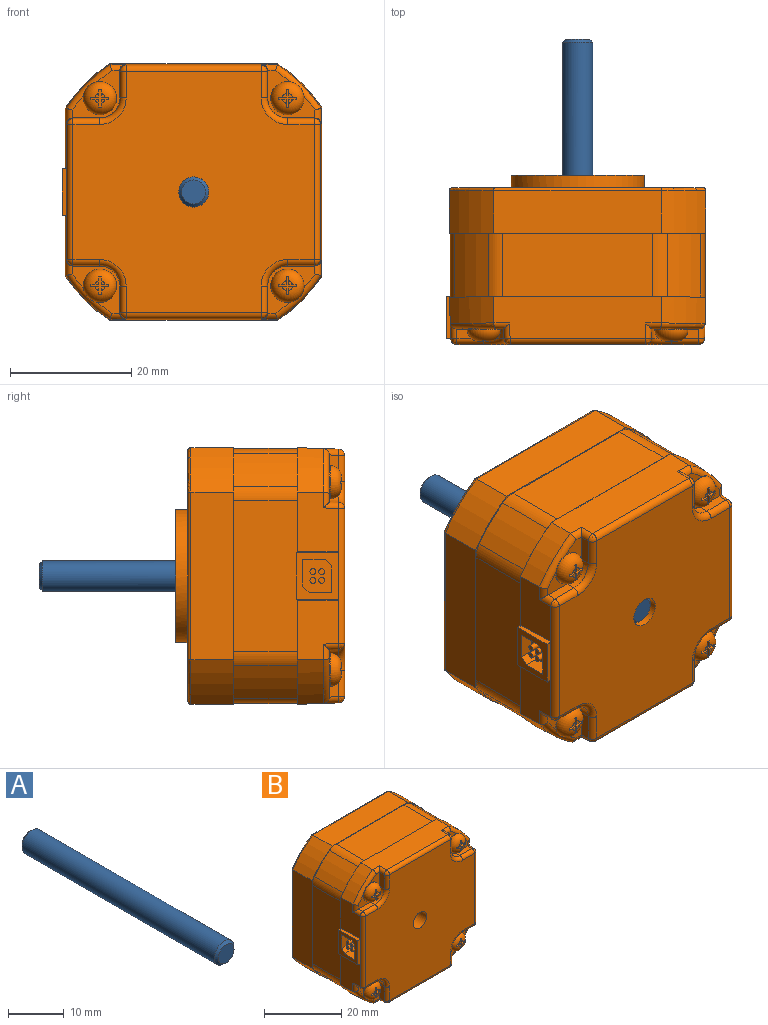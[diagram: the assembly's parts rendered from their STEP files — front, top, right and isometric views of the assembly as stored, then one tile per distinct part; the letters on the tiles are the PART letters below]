
ASSEMBLY  parts=2 mates=1
PART A: 5 faces, bbox 5x49.8x5 mm
  f0: cone r=1mm half-angle=45deg, axis (0,-1,0), area 10.1mm2, adj f2,f3
  f1: cone r=1mm half-angle=45deg, axis (0,1,0), area 10.1mm2, adj f2,f4
  f2: cylinder r=2.5mm len=48.77mm, axis (0,1,0), area 764.7mm2, adj f0,f1
  f3: plane 3.98x3.98mm, normal (0,1,0), area 12.4mm2, adj f0
  f4: plane 3.98x3.98mm, normal (0,-1,0), area 12.4mm2, adj f1
PART B: 249 faces, bbox 46x28.1x46 mm
  f0: cylinder r=0.48mm len=1.93mm, axis (1,0,0), area 5.9mm2, adj f1,f2
  f1: plane 0.97x0.97mm, normal (-1,0,0), area 0.7mm2, adj f0
  f2: plane 5.49x4.85mm, normal (-1,0,0), area 22.5mm2, adj f0,f3,f5,f7,f9,f244,f245,f246
  f3: cylinder r=0.48mm len=1.93mm, axis (1,0,0), area 5.9mm2, adj f2,f4
  f4: plane 0.97x0.97mm, normal (-1,0,0), area 0.7mm2, adj f3
  f5: cylinder r=0.48mm len=1.93mm, axis (1,0,0), area 5.9mm2, adj f2,f6
  f6: plane 0.97x0.97mm, normal (-1,0,0), area 0.7mm2, adj f5
  f7: cylinder r=0.48mm len=1.93mm, axis (1,0,0), area 5.9mm2, adj f2,f8
  f8: plane 0.97x0.97mm, normal (-1,0,0), area 0.7mm2, adj f7
  f9: plane 3.77x2.36mm, normal (0,0,-1), area 8.9mm2, adj f2,f10,f244,f248
  f10: plane 7.62x6.99mm, normal (-1,0,0), area 27.8mm2, adj f9,f11,f241,f242,f243,f244,f245,f246
  f11: plane 7.62x0.79mm, normal (0,-1,0), area 6mm2, adj f10,f12,f241,f243
  f12: plane 27.77x6.84mm, normal (-1,-0.03,0), area 121.2mm2, adj f11,f13,f230,f231,f232,f233,f234,f235
  f13: plane 6.61x1.82mm, normal (0,0,-1), area 11.2mm2, adj f12,f14,f15,f237,f240
  f14: plane 6.61x0.25mm, normal (-1,0,0), area 1.7mm2, adj f13,f15,f240,f243
  f15: plane 1.69x0.25mm, normal (0,-1,0), area 0.4mm2, adj f13,f14,f16,f243
  f16: plane 24.85x10.52mm, normal (-1,0,0), area 261.3mm2, adj f15,f17,f224,f225,f227,f229,f237
  f17: plane 42.42x42.42mm, normal (0,-1,0), area 24.6mm2, adj f16,f18,f19,f20,f21,f22,f23,f24
  f18: cylinder r=25.13mm len=10.52mm, axis (0,1,0), area 82.5mm2, adj f17,f19,f229,f237
  f19: cylinder r=4.01mm len=10.52mm, axis (0,1,0), area 26.6mm2, adj f17,f18,f20,f237
  f20: plane 24.85x10.52mm, normal (0,0,-1), area 261.3mm2, adj f17,f19,f21,f237
  f21: cylinder r=4.01mm len=10.52mm, axis (0,1,0), area 26.6mm2, adj f17,f20,f22,f237
  f22: cylinder r=25.13mm len=10.52mm, axis (0,1,0), area 82.5mm2, adj f17,f21,f23,f237
  f23: cylinder r=4.01mm len=10.52mm, axis (0,1,0), area 26.6mm2, adj f17,f22,f24,f237
  f24: plane 24.85x10.52mm, normal (1,0,0), area 261.3mm2, adj f17,f23,f25,f237
  f25: cylinder r=4.01mm len=10.52mm, axis (0,1,0), area 26.6mm2, adj f17,f24,f26,f237
  f26: cylinder r=25.13mm len=10.52mm, axis (0,1,0), area 82.5mm2, adj f17,f25,f27,f237
  f27: cylinder r=4.01mm len=10.52mm, axis (0,1,0), area 26.6mm2, adj f17,f26,f28,f237
  f28: plane 24.85x10.52mm, normal (0,0,1), area 261.3mm2, adj f17,f27,f29,f237
  f29: cylinder r=4.01mm len=10.52mm, axis (0,1,0), area 26.6mm2, adj f17,f28,f30,f237
  f30: cylinder r=25.13mm len=10.52mm, axis (0,1,0), area 82.5mm2, adj f17,f29,f224,f237
  f31: plane 27.77x7.06mm, normal (0,0,1), area 196.1mm2, adj f17,f32,f217,f223
  f32: cylinder r=0.51mm len=27.77mm, axis (1,0,0), area 22mm2, adj f31,f33,f39,f216
  f33: torus R=24.84mm, axis (0,1,0), area 8.1mm2, adj f32,f34,f39,f223
  f34: cylinder r=0.51mm len=27.77mm, axis (0,0,1), area 22mm2, adj f33,f35,f39,f222
  f35: torus R=24.84mm, axis (0,1,0), area 8.1mm2, adj f34,f36,f39,f221
  f36: cylinder r=0.51mm len=27.77mm, axis (-1,0,0), area 22mm2, adj f35,f37,f39,f220
  f37: torus R=24.84mm, axis (0,1,0), area 8.1mm2, adj f36,f38,f39,f219
  f38: cylinder r=0.51mm len=27.77mm, axis (0,0,-1), area 22mm2, adj f37,f39,f216,f218
  f39: plane 41.4x41.4mm, normal (0,1,0), area 1030.3mm2, adj f32,f33,f34,f35,f36,f37,f38,f40
  f40: cone r=1mm half-angle=45deg, axis (0,1,0), area 2.6mm2, adj f39,f41,f44,f45,f46
  f41: cylinder r=1.23mm len=3.49mm, axis (0,1,0), area -38.1mm2, adj f40,f42,f43,f44,f46
  f42: bspline ~3.05x3.05mm, area 6.4mm2, adj f41,f43,f45
  f43: plane 2.86x2.83mm, normal (0,1,0), area 5.7mm2, adj f41,f42,f45,f46
  f44: bspline ~3.04x3.03mm, area 5.1mm2, adj f40,f41,f45
  f45: cylinder r=1.5mm len=3.76mm, axis (0,1,0), area 3.8mm2, adj f40,f42,f43,f44,f46
  f46: bspline ~4.17x3.53mm, area 17.6mm2, adj f40,f41,f43,f45
  f47: cone r=1mm half-angle=45deg, axis (0,1,0), area 2.6mm2, adj f39,f48,f51,f52,f53
  f48: cylinder r=1.23mm len=3.49mm, axis (0,1,0), area -38.1mm2, adj f47,f49,f50,f51,f53
  f49: bspline ~3.05x3.05mm, area 6.4mm2, adj f48,f50,f52
  f50: plane 2.86x2.83mm, normal (0,1,0), area 5.7mm2, adj f48,f49,f52,f53
  f51: bspline ~3.04x3.03mm, area 5.1mm2, adj f47,f48,f52
  f52: cylinder r=1.5mm len=3.76mm, axis (0,1,0), area 3.8mm2, adj f47,f49,f50,f51,f53
  f53: bspline ~4.17x3.53mm, area 17.6mm2, adj f47,f48,f50,f52
  f54: cone r=1mm half-angle=45deg, axis (0,1,0), area 2.6mm2, adj f39,f55,f58,f59,f60
  f55: cylinder r=1.23mm len=3.49mm, axis (0,1,0), area -38.1mm2, adj f54,f56,f57,f58,f60
  f56: bspline ~3.05x3.05mm, area 6.4mm2, adj f55,f57,f59
  f57: plane 2.86x2.83mm, normal (0,1,0), area 5.7mm2, adj f55,f56,f59,f60
  f58: bspline ~3.04x3.03mm, area 5.1mm2, adj f54,f55,f59
  f59: cylinder r=1.5mm len=3.76mm, axis (0,1,0), area 3.8mm2, adj f54,f56,f57,f58,f60
  f60: bspline ~4.17x3.53mm, area 17.6mm2, adj f54,f55,f57,f59
  f61: cylinder r=13.46mm len=26.92mm, axis (0,1,0), area 43mm2, adj f39,f62
  f62: plane 26.92x26.92mm, normal (0,1,0), area 189.3mm2, adj f61,f63
  f63: cylinder r=11mm len=22mm, axis (0,-1,0), area 175.5mm2, adj f62,f64
  f64: plane 22x22mm, normal (0,1,0), area 314.3mm2, adj f63,f65
  f65: cylinder r=4.57mm len=9.14mm, axis (0,1,0), area 58.4mm2, adj f64,f66
  f66: plane 9.14x9.14mm, normal (0,1,0), area 46.1mm2, adj f65,f67
  f67: cylinder r=2.5mm len=25.91mm, axis (0,1,0), area 406.2mm2, adj f66,f68
  f68: plane 39.91x39.91mm, normal (0,-1,0), area 1280.7mm2, adj f67,f69,f193,f194,f195,f196,f198,f200
  f69: cylinder r=1.02mm len=4.42mm, axis (0,0,1), area 6.9mm2, adj f68,f70,f192,f208
  f70: plane 4.47x1.56mm, normal (1,-0.03,0), area 6.9mm2, adj f69,f71,f190,f191
  f71: plane 7.81x7.81mm, normal (0,-1,0), area 17.4mm2, adj f70,f72,f165,f166,f168,f169,f189,f190
  f72: cylinder r=1.02mm len=2.58mm, axis (-1,0,0), area 3mm2, adj f71,f73,f189,f190
  f73: plane 27.77x6.84mm, normal (0,-0.03,-1), area 176.3mm2, adj f72,f74,f100,f102,f190,f193,f236,f237
  f74: cylinder r=1.02mm len=2.58mm, axis (-1,0,0), area 3mm2, adj f73,f75,f99,f100
  f75: plane 7.81x7.81mm, normal (0,-1,0), area 17.4mm2, adj f74,f76,f77,f78,f79,f99,f100,f234
  f76: plane 4.47x1.56mm, normal (0,-0.03,-1), area 6.9mm2, adj f75,f77,f196,f234
  f77: cone r=0.03mm half-angle=2deg, axis (0,-1,0), area 8.2mm2, adj f75,f76,f78,f195
  f78: plane 4.47x1.56mm, normal (-1,-0.03,0), area 6.9mm2, adj f75,f77,f100,f194
  f79: cylinder r=2.75mm len=5.5mm, axis (0,1,0), area 2.2mm2, adj f75,f80,f98
  f80: torus R=0.84mm, axis (0,1,0), area 37.5mm2, adj f79,f81,f83,f84,f85,f86,f87,f88
  f81: plane 1.56x1.33mm, normal (-1,0,0), area 1.9mm2, adj f80,f82,f83,f84,f97
  f82: plane 3x3mm, normal (0,-1,0), area 2.3mm2, adj f81,f84,f85,f86,f88,f89,f90,f92
  f83: plane 0.62x0.62mm, normal (0,-1,0), area 0.3mm2, adj f80,f81,f84
  f84: plane 1.56x1.33mm, normal (0,0,1), area 1.9mm2, adj f80,f81,f82,f83,f85
  f85: plane 1.44x0.44mm, normal (-1,0,0), area 0.6mm2, adj f80,f82,f84,f86
  f86: plane 1.56x1.33mm, normal (0,0,-1), area 1.9mm2, adj f80,f82,f85,f87,f88
  f87: plane 0.62x0.62mm, normal (0,-1,0), area 0.3mm2, adj f80,f86,f88
  f88: plane 1.56x1.33mm, normal (-1,0,0), area 1.9mm2, adj f80,f82,f86,f87,f89
  f89: plane 1.42x0.41mm, normal (0,0,-1), area 0.6mm2, adj f80,f82,f88,f90
  f90: plane 1.56x1.33mm, normal (1,0,0), area 1.9mm2, adj f80,f82,f89,f91,f92
  f91: plane 0.62x0.62mm, normal (0,-1,0), area 0.3mm2, adj f80,f90,f92
  f92: plane 1.56x1.33mm, normal (0,0,-1), area 1.9mm2, adj f80,f82,f90,f91,f93
  f93: plane 1.44x0.44mm, normal (1,0,0), area 0.6mm2, adj f80,f82,f92,f94
  f94: plane 1.56x1.33mm, normal (0,0,1), area 1.9mm2, adj f80,f82,f93,f95,f96
  f95: plane 0.62x0.62mm, normal (0,-1,0), area 0.3mm2, adj f80,f94,f96
  f96: plane 1.56x1.33mm, normal (1,0,0), area 1.9mm2, adj f80,f82,f94,f95,f97
  f97: plane 1.42x0.41mm, normal (0,0,1), area 0.6mm2, adj f80,f81,f82,f96
  f98: plane 2.3x2.3mm, normal (0,1,0), area 1.1mm2, adj f79,f99
  f99: torus R=24.18mm, axis (0,1,0), area 15.3mm2, adj f74,f75,f98,f235,f236
  f100: cylinder r=1.02mm len=2.55mm, axis (-0.03,1,-0.03), area 3.1mm2, adj f73,f74,f75,f78,f101
  f101: sphere r=1.02mm, area 1mm2, adj f100,f193,f194
  f102: cone r=0.03mm half-angle=2deg, axis (0,1,0), area 44.6mm2, adj f73,f103,f189,f237
  f103: plane 27.77x6.84mm, normal (1,-0.03,0), area 176.3mm2, adj f102,f104,f163,f164,f166,f168,f206,f237
  f104: cylinder r=1.02mm len=2.55mm, axis (-0.03,-1,-0.03), area 3.1mm2, adj f103,f105,f106,f162,f163
  f105: sphere r=1.02mm, area 1mm2, adj f104,f205,f206
  f106: plane 4.47x1.56mm, normal (0,-0.03,1), area 6.9mm2, adj f104,f107,f162,f205
  f107: cone r=0.03mm half-angle=2deg, axis (0,-1,0), area 8.2mm2, adj f106,f108,f162,f204
  f108: plane 4.47x1.56mm, normal (1,-0.03,0), area 6.9mm2, adj f107,f109,f162,f203
  f109: cylinder r=1.02mm len=2.55mm, axis (0.03,1,0.03), area 3.1mm2, adj f108,f110,f111,f140,f162
  f110: sphere r=1.02mm, area 1mm2, adj f109,f202,f203
  f111: plane 27.77x6.84mm, normal (0,-0.03,1), area 176.3mm2, adj f109,f112,f139,f140,f164,f202,f230,f237
  f112: cylinder r=1.02mm len=2.55mm, axis (0.03,-1,-0.03), area 3.1mm2, adj f111,f113,f114,f117,f139
  f113: sphere r=1.02mm, area 1mm2, adj f112,f201,f202
  f114: plane 4.47x1.56mm, normal (-1,-0.03,0), area 6.9mm2, adj f112,f115,f117,f201
  f115: cone r=0.03mm half-angle=2deg, axis (0,-1,0), area 8.2mm2, adj f114,f116,f117,f200
  f116: plane 4.47x1.56mm, normal (0,-0.03,1), area 6.9mm2, adj f115,f117,f198,f232
  f117: plane 7.81x7.81mm, normal (0,-1,0), area 17.4mm2, adj f112,f114,f115,f116,f118,f138,f139,f231
  f118: cylinder r=2.75mm len=5.5mm, axis (0,1,0), area 2.2mm2, adj f117,f119,f137
  f119: torus R=0.84mm, axis (0,1,0), area 37.5mm2, adj f118,f120,f122,f123,f124,f125,f126,f127
  f120: plane 1.56x1.33mm, normal (-1,0,0), area 1.9mm2, adj f119,f121,f122,f123,f136
  f121: plane 3x3mm, normal (0,-1,0), area 2.3mm2, adj f120,f123,f124,f125,f127,f128,f129,f131
  f122: plane 0.62x0.62mm, normal (0,-1,0), area 0.3mm2, adj f119,f120,f123
  f123: plane 1.56x1.33mm, normal (0,0,1), area 1.9mm2, adj f119,f120,f121,f122,f124
  f124: plane 1.44x0.44mm, normal (-1,0,0), area 0.6mm2, adj f119,f121,f123,f125
  f125: plane 1.56x1.33mm, normal (0,0,-1), area 1.9mm2, adj f119,f121,f124,f126,f127
  f126: plane 0.62x0.62mm, normal (0,-1,0), area 0.3mm2, adj f119,f125,f127
  f127: plane 1.56x1.33mm, normal (-1,0,0), area 1.9mm2, adj f119,f121,f125,f126,f128
  f128: plane 1.42x0.41mm, normal (0,0,-1), area 0.6mm2, adj f119,f121,f127,f129
  f129: plane 1.56x1.33mm, normal (1,0,0), area 1.9mm2, adj f119,f121,f128,f130,f131
  f130: plane 0.62x0.62mm, normal (0,-1,0), area 0.3mm2, adj f119,f129,f131
  f131: plane 1.56x1.33mm, normal (0,0,-1), area 1.9mm2, adj f119,f121,f129,f130,f132
  f132: plane 1.44x0.44mm, normal (1,0,0), area 0.6mm2, adj f119,f121,f131,f133
  f133: plane 1.56x1.33mm, normal (0,0,1), area 1.9mm2, adj f119,f121,f132,f134,f135
  f134: plane 0.62x0.62mm, normal (0,-1,0), area 0.3mm2, adj f119,f133,f135
  f135: plane 1.56x1.33mm, normal (1,0,0), area 1.9mm2, adj f119,f121,f133,f134,f136
  f136: plane 1.42x0.41mm, normal (0,0,1), area 0.6mm2, adj f119,f120,f121,f135
  f137: plane 2.3x2.3mm, normal (0,1,0), area 1.1mm2, adj f118,f138
  f138: torus R=24.18mm, axis (0,-1,0), area 15.3mm2, adj f117,f137,f139,f230,f231
  f139: cylinder r=1.02mm len=2.58mm, axis (1,0,0), area 3mm2, adj f111,f112,f117,f138
  f140: cylinder r=1.02mm len=2.58mm, axis (1,0,0), area 3mm2, adj f109,f111,f141,f162
  f141: torus R=24.18mm, axis (0,-1,0), area 15.3mm2, adj f140,f142,f162,f163,f164
  f142: plane 2.3x2.3mm, normal (0,1,0), area 1.1mm2, adj f141,f143
  f143: cylinder r=2.75mm len=5.5mm, axis (0,1,0), area 2.2mm2, adj f142,f144,f162
  f144: torus R=0.84mm, axis (0,1,0), area 37.5mm2, adj f143,f145,f147,f148,f149,f150,f151,f152
  f145: plane 1.56x1.33mm, normal (-1,0,0), area 1.9mm2, adj f144,f146,f147,f148,f161
  f146: plane 3x3mm, normal (0,-1,0), area 2.3mm2, adj f145,f148,f149,f150,f152,f153,f154,f156
  f147: plane 0.62x0.62mm, normal (0,-1,0), area 0.3mm2, adj f144,f145,f148
  f148: plane 1.56x1.33mm, normal (0,0,1), area 1.9mm2, adj f144,f145,f146,f147,f149
  f149: plane 1.44x0.44mm, normal (-1,0,0), area 0.6mm2, adj f144,f146,f148,f150
  f150: plane 1.56x1.33mm, normal (0,0,-1), area 1.9mm2, adj f144,f146,f149,f151,f152
  f151: plane 0.62x0.62mm, normal (0,-1,0), area 0.3mm2, adj f144,f150,f152
  f152: plane 1.56x1.33mm, normal (-1,0,0), area 1.9mm2, adj f144,f146,f150,f151,f153
  f153: plane 1.42x0.41mm, normal (0,0,-1), area 0.6mm2, adj f144,f146,f152,f154
  f154: plane 1.56x1.33mm, normal (1,0,0), area 1.9mm2, adj f144,f146,f153,f155,f156
  f155: plane 0.62x0.62mm, normal (0,-1,0), area 0.3mm2, adj f144,f154,f156
  f156: plane 1.56x1.33mm, normal (0,0,-1), area 1.9mm2, adj f144,f146,f154,f155,f157
  f157: plane 1.44x0.44mm, normal (1,0,0), area 0.6mm2, adj f144,f146,f156,f158
  f158: plane 1.56x1.33mm, normal (0,0,1), area 1.9mm2, adj f144,f146,f157,f159,f160
  f159: plane 0.62x0.62mm, normal (0,-1,0), area 0.3mm2, adj f144,f158,f160
  f160: plane 1.56x1.33mm, normal (1,0,0), area 1.9mm2, adj f144,f146,f158,f159,f161
  f161: plane 1.42x0.41mm, normal (0,0,1), area 0.6mm2, adj f144,f145,f146,f160
  f162: plane 7.81x7.81mm, normal (0,-1,0), area 17.4mm2, adj f104,f106,f107,f108,f109,f140,f141,f143
  f163: cylinder r=1.02mm len=2.58mm, axis (0,0,-1), area 3mm2, adj f103,f104,f141,f162
  f164: cone r=0.03mm half-angle=2deg, axis (0,1,0), area 44.6mm2, adj f103,f111,f141,f237
  f165: plane 4.47x1.56mm, normal (0,-0.03,-1), area 6.9mm2, adj f71,f166,f191,f207
  f166: cylinder r=1.02mm len=2.55mm, axis (0.03,1,-0.03), area 3.1mm2, adj f71,f103,f165,f167,f168
  f167: sphere r=1.02mm, area 1mm2, adj f166,f206,f207
  f168: cylinder r=1.02mm len=2.58mm, axis (0,0,-1), area 3mm2, adj f71,f103,f166,f189
  f169: cylinder r=2.75mm len=5.5mm, axis (0,1,0), area 2.2mm2, adj f71,f170,f171
  f170: plane 2.3x2.3mm, normal (0,1,0), area 1.1mm2, adj f169,f189
  f171: torus R=0.84mm, axis (0,1,0), area 37.5mm2, adj f169,f172,f174,f175,f176,f177,f178,f179
  f172: plane 1.56x1.33mm, normal (-1,0,0), area 1.9mm2, adj f171,f173,f174,f175,f188
  f173: plane 3x3mm, normal (0,-1,0), area 2.3mm2, adj f172,f175,f176,f177,f179,f180,f181,f183
  f174: plane 0.62x0.62mm, normal (0,-1,0), area 0.3mm2, adj f171,f172,f175
  f175: plane 1.56x1.33mm, normal (0,0,1), area 1.9mm2, adj f171,f172,f173,f174,f176
  f176: plane 1.44x0.44mm, normal (-1,0,0), area 0.6mm2, adj f171,f173,f175,f177
  f177: plane 1.56x1.33mm, normal (0,0,-1), area 1.9mm2, adj f171,f173,f176,f178,f179
  f178: plane 0.62x0.62mm, normal (0,-1,0), area 0.3mm2, adj f171,f177,f179
  f179: plane 1.56x1.33mm, normal (-1,0,0), area 1.9mm2, adj f171,f173,f177,f178,f180
  f180: plane 1.42x0.41mm, normal (0,0,-1), area 0.6mm2, adj f171,f173,f179,f181
  f181: plane 1.56x1.33mm, normal (1,0,0), area 1.9mm2, adj f171,f173,f180,f182,f183
  f182: plane 0.62x0.62mm, normal (0,-1,0), area 0.3mm2, adj f171,f181,f183
  f183: plane 1.56x1.33mm, normal (0,0,-1), area 1.9mm2, adj f171,f173,f181,f182,f184
  f184: plane 1.44x0.44mm, normal (1,0,0), area 0.6mm2, adj f171,f173,f183,f185
  f185: plane 1.56x1.33mm, normal (0,0,1), area 1.9mm2, adj f171,f173,f184,f186,f187
  f186: plane 0.62x0.62mm, normal (0,-1,0), area 0.3mm2, adj f171,f185,f187
  f187: plane 1.56x1.33mm, normal (1,0,0), area 1.9mm2, adj f171,f173,f185,f186,f188
  f188: plane 1.42x0.41mm, normal (0,0,1), area 0.6mm2, adj f171,f172,f173,f187
  f189: torus R=24.18mm, axis (0,-1,0), area 15.3mm2, adj f71,f72,f102,f168,f170
  f190: cylinder r=1.02mm len=2.55mm, axis (-0.03,-1,0.03), area 3.1mm2, adj f70,f71,f72,f73,f192
  f191: cone r=0.03mm half-angle=2deg, axis (0,-1,0), area 8.2mm2, adj f70,f71,f165,f208
  f192: sphere r=1.02mm, area 1mm2, adj f69,f190,f193
  f193: cylinder r=1.02mm len=22.33mm, axis (1,0,0), area 34.9mm2, adj f68,f73,f101,f192
  f194: cylinder r=1.02mm len=4.42mm, axis (0,0,-1), area 6.9mm2, adj f68,f78,f101,f195
  f195: torus R=4.37mm, axis (0,1,0), area 9.2mm2, adj f68,f77,f194,f196
  f196: cylinder r=1.02mm len=4.42mm, axis (1,0,0), area 6.9mm2, adj f68,f76,f195,f197
  f197: sphere r=1.02mm, area 1mm2, adj f196,f233,f234
  f198: cylinder r=1.02mm len=4.42mm, axis (-1,0,0), area 6.9mm2, adj f68,f116,f199,f200
  f199: sphere r=1.02mm, area 1mm2, adj f198,f232,f233
  f200: torus R=4.37mm, axis (0,1,0), area 9.2mm2, adj f68,f115,f198,f201
  f201: cylinder r=1.02mm len=4.42mm, axis (0,0,-1), area 6.9mm2, adj f68,f113,f114,f200
  f202: cylinder r=1.02mm len=22.33mm, axis (-1,0,0), area 34.9mm2, adj f68,f110,f111,f113
  f203: cylinder r=1.02mm len=4.42mm, axis (0,0,1), area 6.9mm2, adj f68,f108,f110,f204
  f204: torus R=4.37mm, axis (0,1,0), area 9.2mm2, adj f68,f107,f203,f205
  f205: cylinder r=1.02mm len=4.42mm, axis (-1,0,0), area 6.9mm2, adj f68,f105,f106,f204
  f206: cylinder r=1.02mm len=22.33mm, axis (0,0,1), area 34.9mm2, adj f68,f103,f105,f167
  f207: cylinder r=1.02mm len=4.42mm, axis (1,0,0), area 6.9mm2, adj f68,f165,f167,f208
  f208: torus R=4.37mm, axis (0,1,0), area 9.2mm2, adj f68,f69,f191,f207
  f209: cone r=1mm half-angle=45deg, axis (0,1,0), area 2.6mm2, adj f39,f210,f213,f214,f215
  f210: cylinder r=1.23mm len=3.49mm, axis (0,1,0), area -28.7mm2, adj f209,f211,f212,f213,f215
  f211: bspline ~3.05x3.05mm, area 6.4mm2, adj f210,f212,f214
  f212: plane 2.86x2.83mm, normal (0,1,0), area 5.7mm2, adj f210,f211,f214,f215
  f213: bspline ~3.04x3.03mm, area 5.1mm2, adj f209,f210,f214
  f214: cylinder r=1.5mm len=3.76mm, axis (0,1,0), area 3.8mm2, adj f209,f211,f212,f213,f215
  f215: bspline ~4.17x3.53mm, area 17.6mm2, adj f209,f210,f212,f214
  f216: torus R=24.84mm, axis (0,1,0), area 8.1mm2, adj f32,f38,f39,f217
  f217: cylinder r=25.35mm len=7.33mm, axis (0,1,0), area 73.7mm2, adj f17,f31,f216,f218
  f218: plane 27.77x7.06mm, normal (1,0,0), area 196.1mm2, adj f17,f38,f217,f219
  f219: cylinder r=25.35mm len=7.33mm, axis (0,1,0), area 73.7mm2, adj f17,f37,f218,f220
  f220: plane 27.77x7.06mm, normal (0,0,-1), area 196.1mm2, adj f17,f36,f219,f221
  f221: cylinder r=25.35mm len=7.33mm, axis (0,1,0), area 73.7mm2, adj f17,f35,f220,f222
  f222: plane 27.77x7.06mm, normal (-1,0,0), area 196.1mm2, adj f17,f34,f221,f223
  f223: cylinder r=25.35mm len=7.33mm, axis (0,1,0), area 73.7mm2, adj f17,f31,f33,f222
  f224: cylinder r=4.01mm len=10.52mm, axis (0,1,0), area 26.6mm2, adj f16,f17,f30,f237
  f225: plane 7.62x0.13mm, normal (0,1,0), area 1mm2, adj f16,f226,f241,f243
  f226: plane 7.62x0.19mm, normal (1,0.03,0), area 1.4mm2, adj f225,f241,f242,f243
  f227: plane 1.69x0.25mm, normal (0,-1,0), area 0.4mm2, adj f16,f228,f238,f241
  f228: plane 6.61x0.25mm, normal (-1,0,0), area 1.7mm2, adj f227,f238,f239,f241
  f229: cylinder r=4.01mm len=10.52mm, axis (0,1,0), area 26.6mm2, adj f16,f17,f18,f237
  f230: cone r=0.03mm half-angle=2deg, axis (0,1,0), area 44.6mm2, adj f12,f111,f138,f237
  f231: cylinder r=1.02mm len=2.58mm, axis (0,0,1), area 3mm2, adj f12,f117,f138,f232
  f232: cylinder r=1.02mm len=2.55mm, axis (-0.03,1,0.03), area 3.1mm2, adj f12,f116,f117,f199,f231
  f233: cylinder r=1.02mm len=22.33mm, axis (0,0,-1), area 34.9mm2, adj f12,f68,f197,f199
  f234: cylinder r=1.02mm len=2.55mm, axis (0.03,-1,0.03), area 3.1mm2, adj f12,f75,f76,f197,f235
  f235: cylinder r=1.02mm len=2.58mm, axis (0,0,1), area 3mm2, adj f12,f75,f99,f234
  f236: cone r=0.03mm half-angle=2deg, axis (0,1,0), area 44.6mm2, adj f12,f73,f99,f237
  f237: plane 42.42x42.42mm, normal (0,1,0), area 23.6mm2, adj f12,f13,f16,f18,f19,f20,f21,f22
  f238: plane 6.61x1.82mm, normal (0,0,1), area 11.2mm2, adj f12,f227,f228,f237,f239
  f239: plane 1.59x0.25mm, normal (0,1,0), area 0.4mm2, adj f12,f228,f238,f241
  f240: plane 1.59x0.25mm, normal (0,1,0), area 0.4mm2, adj f12,f13,f14,f243
  f241: plane 6.99x2.36mm, normal (0,0,-1), area 15.9mm2, adj f10,f11,f12,f225,f226,f227,f228,f239
  f242: plane 7.62x0.54mm, normal (0,1,0), area 4.1mm2, adj f10,f226,f241,f243
  f243: plane 6.99x2.36mm, normal (0,0,1), area 15.9mm2, adj f10,f11,f12,f14,f15,f225,f226,f240
  f244: plane 2.36x1.08mm, normal (0,0.71,-0.71), area 3.6mm2, adj f2,f9,f10,f245
  f245: plane 4.41x2.36mm, normal (0,1,0), area 10.4mm2, adj f2,f10,f244,f246
  f246: plane 3.77x2.36mm, normal (0,0,1), area 8.9mm2, adj f2,f10,f245,f247
  f247: plane 2.36x1.08mm, normal (0,-0.71,0.71), area 3.6mm2, adj f2,f10,f246,f248
  f248: plane 4.41x2.36mm, normal (0,-1,0), area 10.4mm2, adj f2,f9,f10,f247
PLACE A t=(45.09,-116.59,121.64)mm
PLACE B t=(45.09,-117.25,121.64)mm
MATE revolute A.f0 <-> B.f63  axis (0,1,0) through (-134.9,-77.32,-57.1)mm
